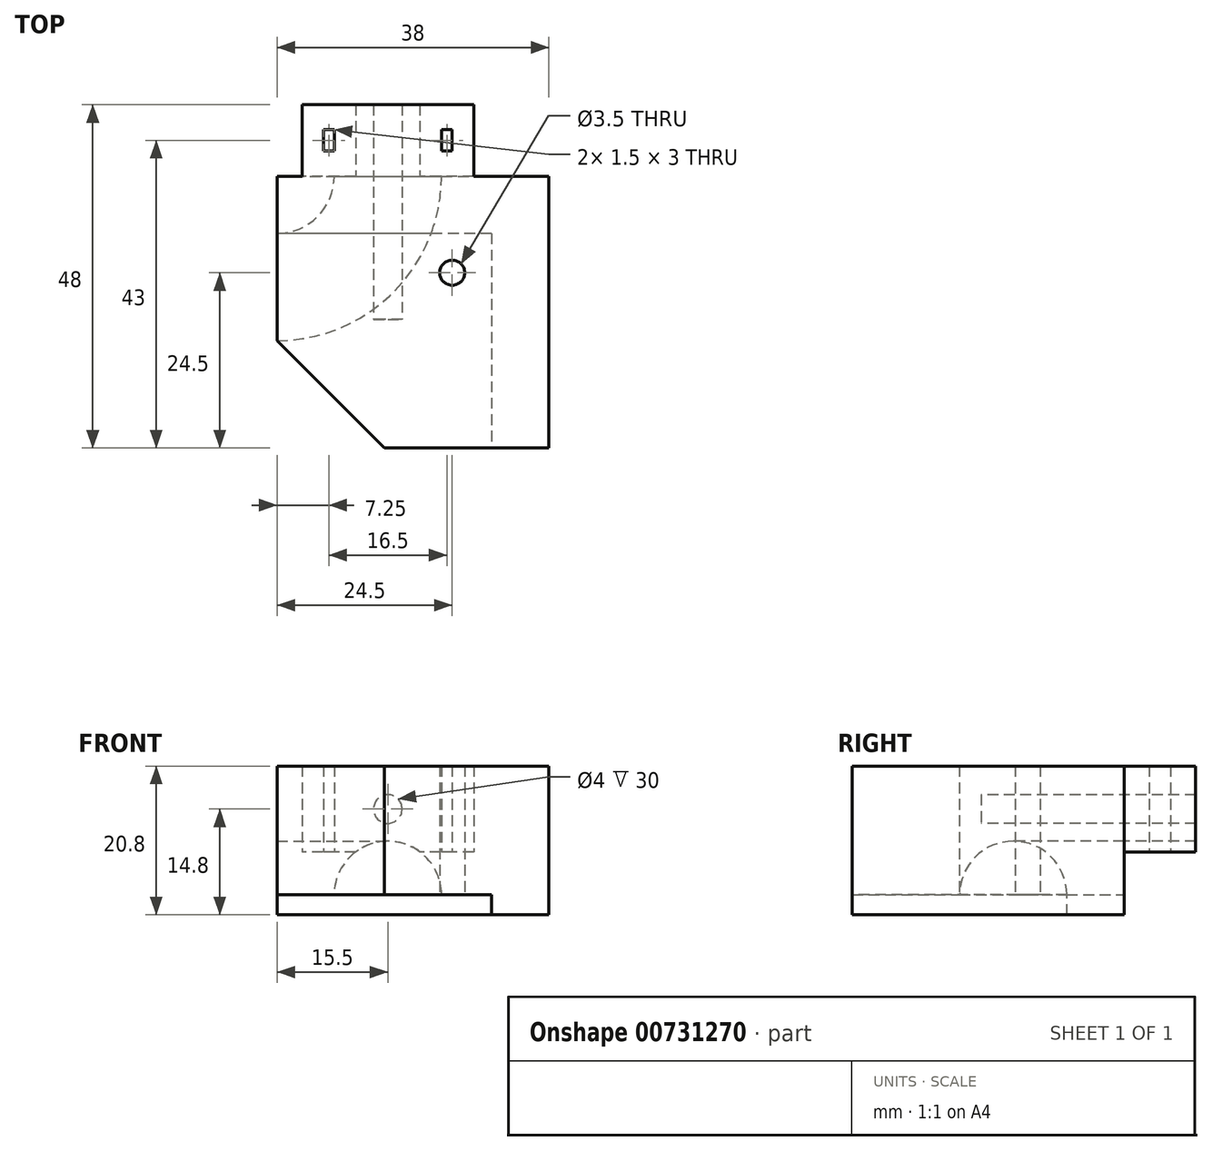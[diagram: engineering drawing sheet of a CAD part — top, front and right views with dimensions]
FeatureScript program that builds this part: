
annotation { "Feature Type Name" : "Feature", "Feature Type Description" : "" }
export const myFeature = defineFeature(function(context is Context, id is Id, definition is map)
    precondition{}
    {
        {
            var Q0;
            Q0=qCreatedBy(makeId("Top.planeOp"),FACE);
            var sketch = newSketch(context, id + "F0", { "sketchPlane" : qUnion([Q0])});
            skCircle(sketch, "E0", {"center": v(0, 0) * mm, "radius": 1.75 * mm});
            skCircle(sketch, "E1", {"center": v(0, 0) * mm, "radius": 5.5 * mm, "construction": true});
            skLineSegment(sketch, "E2", {"start": v(5.5, 0) * mm, "end": v(5.5, -24.5) * mm});
            skLineSegment(sketch, "E3", {"start": v(0, 5.5) * mm, "end": v(-24.5, 5.5) * mm});
            skLineSegment(sketch, "E4", {"start": v(-24.5, 5.5) * mm, "end": v(-24.5, -9.5) * mm});
            skLineSegment(sketch, "E5", {"start": v(5.5, -24.5) * mm, "end": v(-9.5, -24.5) * mm});
            skLineSegment(sketch, "E6", {"start": v(-9.5, -24.5) * mm, "end": v(-24.5, -9.5) * mm});
            skLineSegment(sketch, "E7", {"start": v(0, 5.5) * mm, "end": v(5.5, 5.5) * mm});
            skLineSegment(sketch, "E8", {"start": v(5.5, 5.5) * mm, "end": v(5.5, 0) * mm});
            skLineSegment(sketch, "E9.0", {"start": v(0, 13.5) * mm, "end": v(-24.5, 13.5) * mm});
            skLineSegment(sketch, "E9.1", {"start": v(0, 13.5) * mm, "end": v(13.5, 13.5) * mm});
            skLineSegment(sketch, "E9.2", {"start": v(13.5, 13.5) * mm, "end": v(13.5, 0) * mm});
            skLineSegment(sketch, "E9.3", {"start": v(13.5, 0) * mm, "end": v(13.5, -24.5) * mm});
            skLineSegment(sketch, "E10", {"start": v(-24.5, 13.5) * mm, "end": v(-24.5, 5.5) * mm});
            skLineSegment(sketch, "E11", {"start": v(5.5, -24.5) * mm, "end": v(13.5, -24.5) * mm});
            skSolve(sketch);
        }
        {
            var Q0;
            Q0=makeQuery(id+"F0.imprint","IMPRINT",FACE,{"disambiguationData":[TD([[makeQuery(id+"F0.imprint","IMPRINT",EDGE,{"derivedFrom":sQuery(id+"F0.wireOp",EDGE,"E0")}),-1.0]])]});
            var Q1;
            Q1=makeQuery(id+"F0.imprint","IMPRINT",FACE,{"disambiguationData":[TD([[makeQuery(id+"F0.imprint","IMPRINT",EDGE,{"derivedFrom":sQuery(id+"F0.wireOp",EDGE,"E2")}),1.0]])]});
            extrude(context, id + "F1", {"entities" : qUnion([Q0, Q1]), "depth" : 18 * mm, "offsetDistance" : 25 * mm});
        }
        {
            var Q0;
            Q0=makeQuery(id+"F0.imprint","IMPRINT",FACE,{"disambiguationData":[TD([[makeQuery(id+"F0.imprint","IMPRINT",EDGE,{"derivedFrom":sQuery(id+"F0.wireOp",EDGE,"E2")}),1.0]])]});
            extrude(context, id + "F2", {"entities" : qUnion([Q0]), "operationType" : NewBodyOperationType.ADD, "oppositeDirection" : true, "depth" : 2.8 * mm, "offsetDistance" : 25 * mm});
        }
        {
            var Q0;
            Q0=makeQuery(id+"F0.imprint","IMPRINT",FACE,{"disambiguationData":[TD([[makeQuery(id+"F0.imprint","IMPRINT",EDGE,{"derivedFrom":sQuery(id+"F0.wireOp",EDGE,"E0")}),-1.0]])]});
            var sketch = newSketch(context, id + "F3", { "sketchPlane" : qUnion([Q0])});
            skLineSegment(sketch, "E12.0", {"start": v(-24.5, 13.5) * mm, "end": v(-24.5, 5.5) * mm});
            skLineSegment(sketch, "E13.0", {"start": v(-24.5, 5.5) * mm, "end": v(-24.5, -9.5) * mm});
            skPoint(sketch, "E14", {"position": v(-24.5, -2) * mm});
            skArc(sketch, "E15", {"start": v(-24.5, -2) * mm, "mid": v(-13.54, 2.54) * mm, "end": v(-9, 13.5) * mm});
            skLineSegment(sketch, "E16.0", {"start": v(-24.5, 13.5) * mm, "end": v(13.5, 13.5) * mm});
            skSolve(sketch);
        }
        {
            var Q0;
            {var subQ0=sQuery(id+"F0.wireOp",EDGE,"E10");Q0=makeQuery(id+"F2.boolean.opBoolean","MERGE",FACE,{"derivedFrom":[makeQuery(id+"F1.opExtrude","SWEPT_FACE",FACE,{"disambiguationData":[OSD([sQuery(id+"F0.wireOp",EDGE,"E4"),subQ0])]}),makeQuery(id+"F2.opExtrude","SWEPT_FACE",FACE,{"disambiguationData":[OSD([subQ0])]})]});}
            var sketch = newSketch(context, id + "F4", { "sketchPlane" : qUnion([Q0])});
            skPoint(sketch, "E17.0", {"position": v(2, 0) * mm});
            skArc(sketch, "E18", {"start": v(9.5, 0) * mm, "mid": v(2, 7.5) * mm, "end": v(-5.5, 0) * mm});
            skLineSegment(sketch, "E19.0", {"start": v(-5.5, 0) * mm, "end": v(9.5, 0) * mm});
            skSolve(sketch);
        }
        {
            var Q0;
            {var subQ0=sQuery(id+"F4.wireOp",EDGE,"E18");Q0=makeQuery(id+"F4.imprint","IMPRINT",FACE,{"disambiguationData":[TD([[makeQuery(id+"F4.imprint","IMPRINT",EDGE,{"derivedFrom":subQ0}),1.0]])]});}
            var Q1;
            Q1=sQuery(id+"F3.wireOp",EDGE,"E15");
            sweep(context, id + "F5", {"operationType" : NewBodyOperationType.REMOVE, "profiles" : qUnion([Q0]), "path" : qUnion([Q1])});
        }
        {
            var Q0;
            {var subQ0=sQuery(id+"F0.wireOp",EDGE,"E9.1");var subQ1=sQuery(id+"F0.wireOp",EDGE,"E9.0");Q0=makeQuery(id+"F2.boolean.opBoolean","MERGE",FACE,{"derivedFrom":[makeQuery(id+"F1.opExtrude","SWEPT_FACE",FACE,{"disambiguationData":[OSD([subQ1,subQ0])]}),makeQuery(id+"F2.opExtrude","SWEPT_FACE",FACE,{"disambiguationData":[OSD([subQ1,subQ0])]})]});}
            var sketch = newSketch(context, id + "F6", { "sketchPlane" : qUnion([Q0])});
            skLineSegment(sketch, "E20.0", {"start": v(1.5, 0) * mm, "end": v(1.5, 0) * mm});
            skLineSegment(sketch, "E21.0", {"start": v(24.5, 18) * mm, "end": v(-13.5, 18) * mm});
            skLineSegment(sketch, "E22", {"start": v(9, 0) * mm, "end": v(9, 18) * mm, "construction": true});
            skCircle(sketch, "E23", {"center": v(9, 12) * mm, "radius": 2 * mm});
            skLineSegment(sketch, "E24.bottom", {"start": v(-3, 18) * mm, "end": v(21, 18) * mm});
            skLineSegment(sketch, "E24.top", {"start": v(-3, 6) * mm, "end": v(4.5, 6) * mm});
            skLineSegment(sketch, "E24.left", {"start": v(-3, 18) * mm, "end": v(-3, 6) * mm});
            skLineSegment(sketch, "E24.right", {"start": v(21, 18) * mm, "end": v(21, 6) * mm});
            skLineSegment(sketch, "E25.trimOffspring", {"start": v(13.5, 6) * mm, "end": v(21, 6) * mm});
            skSolve(sketch);
        }
        {
            var Q0;
            Q0=makeQuery(id+"F6.imprint","IMPRINT",FACE,{"disambiguationData":[TD([[makeQuery(id+"F6.imprint","IMPRINT",EDGE,{"derivedFrom":sQuery(id+"F6.wireOp",EDGE,"E23")}),-1.0]])]});
            extrude(context, id + "F7", {"entities" : qUnion([Q0]), "operationType" : NewBodyOperationType.ADD, "depth" : 10 * mm, "offsetDistance" : 25 * mm});
        }
        {
            var Q0;
            {var subQ0=sQuery(id+"F0.wireOp",EDGE,"E9.1");var subQ1=sQuery(id+"F0.wireOp",EDGE,"E9.0");Q0=makeQuery(id+"F7.boolean.opBoolean","SPLIT",FACE,{"disambiguationData":[TD([makeQuery(id+"F7.opExtrude","SWEPT_FACE",FACE,{"disambiguationData":[OSD([sQuery(id+"F6.wireOp",EDGE,"E23")])]})])],"derivedFrom":makeQuery(id+"F2.boolean.opBoolean","MERGE",FACE,{"derivedFrom":[makeQuery(id+"F1.opExtrude","SWEPT_FACE",FACE,{"disambiguationData":[OSD([subQ1,subQ0])]}),makeQuery(id+"F2.opExtrude","SWEPT_FACE",FACE,{"disambiguationData":[OSD([subQ1,subQ0])]})]})});}
            extrude(context, id + "F8", {"entities" : qUnion([Q0]), "operationType" : NewBodyOperationType.REMOVE, "oppositeDirection" : true, "depth" : 20 * mm, "offsetDistance" : 25 * mm});
        }
        {
            var Q0;
            Q0=makeQuery(id+"F7.opExtrude","SWEPT_FACE",FACE,{"disambiguationData":[OSD([sQuery(id+"F6.wireOp",EDGE,"E25.trimOffspring")])]});
            var sketch = newSketch(context, id + "F9", { "sketchPlane" : qUnion([Q0])});
            skLineSegment(sketch, "E26.1.0", {"start": v(3, -13.5) * mm, "end": v(-4.5, -13.5) * mm});
            skLineSegment(sketch, "E26.1.1", {"start": v(-4.5, -13.5) * mm, "end": v(-4.5, -23.5) * mm});
            skLineSegment(sketch, "E26.1.2", {"start": v(-4.5, -23.5) * mm, "end": v(3, -23.5) * mm});
            skLineSegment(sketch, "E26.1.3", {"start": v(3, -23.5) * mm, "end": v(3, -13.5) * mm});
            skLineSegment(sketch, "E27.1", {"start": v(-13.5, -13.5) * mm, "end": v(-21, -13.5) * mm});
            skLineSegment(sketch, "E28.0", {"start": v(-13.5, -23.5) * mm, "end": v(-13.5, -13.5) * mm});
            skLineSegment(sketch, "E29.0", {"start": v(-21, -23.5) * mm, "end": v(-21, -13.5) * mm});
            skLineSegment(sketch, "E30.0", {"start": v(-13.5, -23.5) * mm, "end": v(-21, -23.5) * mm});
            skLineSegment(sketch, "E31.bottom", {"start": v(-16.5, -20) * mm, "end": v(-18, -20) * mm});
            skLineSegment(sketch, "E31.top", {"start": v(-16.5, -17) * mm, "end": v(-18, -17) * mm});
            skLineSegment(sketch, "E31.left", {"start": v(-16.5, -20) * mm, "end": v(-16.5, -17) * mm});
            skLineSegment(sketch, "E31.right", {"start": v(-18, -20) * mm, "end": v(-18, -17) * mm});
            skPoint(sketch, "E31.middle", {"position": v(-17.25, -18.5) * mm});
            skPoint(sketch, "E31.middle.positionSnap0", {"position": v(-21, -18.5) * mm});
            skPoint(sketch, "E31.middle.positionSnap1", {"position": v(-17.25, -23.5) * mm});
            skPoint(sketch, "E31.centerSnap0", {"position": v(-21, -18.5) * mm});
            skPoint(sketch, "E31.centerSnap1", {"position": v(-17.25, -23.5) * mm});
            skLineSegment(sketch, "E32.bottom", {"start": v(0, -20) * mm, "end": v(-1.5, -20) * mm});
            skLineSegment(sketch, "E32.top", {"start": v(0, -17) * mm, "end": v(-1.5, -17) * mm});
            skLineSegment(sketch, "E32.left", {"start": v(0, -20) * mm, "end": v(0, -17) * mm});
            skLineSegment(sketch, "E32.right", {"start": v(-1.5, -20) * mm, "end": v(-1.5, -17) * mm});
            skPoint(sketch, "E32.middle", {"position": v(-0.75, -18.5) * mm});
            skPoint(sketch, "E32.middle.positionSnap0", {"position": v(-0.75, -23.5) * mm});
            skPoint(sketch, "E32.middle.positionSnap1", {"position": v(-4.5, -18.5) * mm});
            skPoint(sketch, "E32.centerSnap0", {"position": v(-0.75, -23.5) * mm});
            skPoint(sketch, "E32.centerSnap1", {"position": v(-4.5, -18.5) * mm});
            skSolve(sketch);
        }
        {
            var Q0;
            Q0=makeQuery(id+"F9.imprint","IMPRINT",FACE,{"disambiguationData":[TD([[makeQuery(id+"F9.imprint","IMPRINT",EDGE,{"derivedFrom":sQuery(id+"F9.wireOp",EDGE,"E31.bottom")}),-1.0]])]});
            var Q1;
            Q1=makeQuery(id+"F9.imprint","IMPRINT",FACE,{"disambiguationData":[TD([[makeQuery(id+"F9.imprint","IMPRINT",EDGE,{"derivedFrom":sQuery(id+"F9.wireOp",EDGE,"E32.bottom")}),-1.0]])]});
            extrude(context, id + "F10", {"entities" : qUnion([Q0, Q1]), "operationType" : NewBodyOperationType.REMOVE, "oppositeDirection" : true, "depth" : 25 * mm, "offsetDistance" : 25 * mm});
        }
    });
